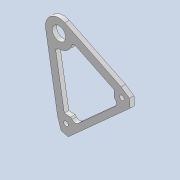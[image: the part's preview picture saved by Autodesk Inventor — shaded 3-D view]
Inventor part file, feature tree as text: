
AUTODESK INVENTOR PART (.ipt)
format: ipt  version: 2020 (Build 240168000, 168)  size: 141,824 bytes
history: native  units: mm
features: other x4, extrude x2, sketch x2, reference x2, chamfer x1, fillet x1, projected_geometry x1
ambient origin geometry x8: Origin, YZ Plane, XZ Plane, XY Plane, X Axis, Y Axis, Z Axis, Center Point
bodies: Solid1 (feature_tree)
feature tree (13):
  extrude  "Extrusion1"  Depth=2.0mm
  chamfer  "Chamfer1"  Distance=2.0mm
  extrude  "Extrusion2"  Depth=2.0mm
  fillet  "Fillet1"  Radius=2.0mm
  sketch  "Sketch1"  dims[d0=6.0mm d1=12.0mm d2=2.0mm d3=0.0mm]
  reference  "Reference1"
  reference  "Reference2"
  sketch  "Sketch2"  dims[d4=3.0mm d5=2.0mm d6=45.0deg d7=2.0mm d8=2.0mm d9=2.0mm d10=0.0mm d11=1.0mm]
  projected_geometry  "Projected Loop1"
  parser-record x1  (decoder bookkeeping rows leaked as tree rows — omitted from the tree; the rows remain in map.json)
  other  "driver_ass_1.iam"
  other  "stand_2:1"
  other  "driver_wheel_1:2"
note: 1 file-system path scrubbed to <path> (originals preserved in map.json)
